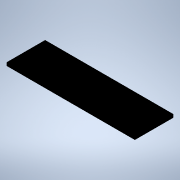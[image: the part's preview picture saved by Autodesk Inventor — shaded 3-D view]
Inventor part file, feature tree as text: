
AUTODESK INVENTOR PART (.ipt)
format: ipt  version: 2022 (Build 260153000, 153)  size: 103,424 bytes
history: native  units: mm
features: other x1, extrude x1, chamfer x1, sketch x1
ambient origin geometry x8: Origin, YZ Plane, XZ Plane, XY Plane, X Axis, Y Axis, Z Axis, Center Point
bodies: Body1 (feature_tree)
feature tree (4):
  other  "ソリッド1"
  extrude  "押し出し1"  Depth=80.0mm
  chamfer  "面取り3"  Distance=24.0mm
  sketch  "スケッチ1"
